# Revit family: Barrera optica lineal de deteccion de incendios_Aguilera Electronica
name_source: partatom
category: Dispositivos de alarma de incendios
units: mm (PartAtom-declared; Revit-internal decimal feet)

## family parameters
Anfitrión = Cara
Compartido = No
Corte con vacíos al cargar = No
Cota de conector redondo = Diámetro de uso
Mantener orientación de anotación = Sí
Número OmniClass = 23.85.30.21.11.11.11
Punto de cálculo de habitación = No
Tipo de pieza = Normal
Título OmniClass = Smoke Detectors

## types (1)
- Barrera óptica lineal de detección de incendios
    Altura = 180 mm  [stored 0.590551 ft]
    Ancho = 134 mm
    Comentarios de tipo = Auto-Alignment™ en un minuto.
Todos los detectores de haz reflectante se pueden alinear en un minuto.
Building Movement Tracking™.
Los detectores de haz reflectante pueden detectar el movimiento de los edificios de forma automática para mantener una alineación óptima durante toda su vida útil. Se minimizan las alarmas no deseadas Light Cancellation Technology™.
La tecnología patentada de Fireray bloquea de forma activa la luz ambiental del sol o fuentes artificiales y permite que los detectores de haz se instalen en tragaluces y atrios de vidrio sin desencadenar alarmas no deseadas.
    Descripción = Sistema de detección lineal diseñado de forma inteligente que se puede adaptar a una variedad de exigentes aplicaciones. Contiene tecnología única desarrollada para proporcionar la mejor protección y facilidad de uso.
Principio de funcionamiento:
Un detector de humo de haz óptico proyecta un haz de luz infrarroja desde un transmisor a un reflector (solo necesita cableado en un extremo). Cuando las partículas de humo bloquean parcialmente el haz y reducen la señal, el detector desencadena una alarma de incendio. Distancia máxima 120 metros.
    Diámetro = 99 mm  [stored 0.324803 ft]
    Elevación por defecto = 400 mm  [stored 1.31234 ft]
    Fabricante = Aguilera Electrónica
    Modelo = AE/BFONE
    Profundidad = 151 mm  [stored 0.495407 ft]
    Radio = 50 mm
    Símbolo = Sí
    Símbolo texto modelo = Sí
    URL = https://aguilera.es

note: [stored X ft] marks values corroborated as IEEE doubles in the binary element streams (Revit-internal decimal feet)
